FCSTD DOCUMENT  (FreeCAD 0.20R29177 +426 (Git))
Label: sketching
License: All rights reserved
LicenseURL: http://en.wikipedia.org/wiki/All_rights_reserved
objects: Sketcher::SketchObject×1
note: 1 computed .brp shape members not serialized (recipe doc carries the construction recipe); baked Part::Feature solids carry a one-line shape summary decoded from their .brp

FEATURE [Sketcher::SketchObject] Sketch
  FullyConstrained = false
  sketch-geometry (15):
    g0: LineSegment StartX=0 StartY=0 StartZ=0 EndX=-26.386 EndY=-14.4782 EndZ=0
    g1: LineSegment StartX=0 StartY=0 StartZ=0 EndX=-27.4681 EndY=14.59 EndZ=0
    g2: LineSegment StartX=0 StartY=0 StartZ=0 EndX=20.6994 EndY=22.0227 EndZ=0
    g3: LineSegment StartX=0 StartY=0 StartZ=0 EndX=30.9074 EndY=-5.00945 EndZ=0
    g4: LineSegment StartX=0 StartY=0 StartZ=0 EndX=5.19849 EndY=-29.7732 EndZ=0
    g5: Circle CenterX=0 CenterY=0 CenterZ=0 NormalX=0 NormalY=0 NormalZ=1 AngleXU=0 Radius=10.5414
    g6: ArcOfCircle CenterX=-26.386 CenterY=-14.4782 CenterZ=0 NormalX=0 NormalY=0 NormalZ=1 AngleXU=0 Radius=6.41713 StartAngle=2.35262 EndAngle=5.5881
    g7: ArcOfCircle CenterX=5.19849 CenterY=-29.7732 CenterZ=0 NormalX=0 NormalY=0 NormalZ=1 AngleXU=0 Radius=6.93275 StartAngle=3.33364 EndAngle=6.45538
    g8: ArcOfCircle CenterX=30.9074 CenterY=-5.00945 CenterZ=0 NormalX=0 NormalY=0 NormalZ=1 AngleXU=0 Radius=7.77119 StartAngle=4.39064 EndAngle=7.83271
    g9: ArcOfCircle CenterX=20.6994 CenterY=22.0227 CenterZ=0 NormalX=0 NormalY=0 NormalZ=1 AngleXU=0 Radius=9.12477 StartAngle=5.58579 EndAngle=8.96771
    g10: ArcOfCircle CenterX=-27.4681 CenterY=14.59 CenterZ=0 NormalX=0 NormalY=0 NormalZ=1 AngleXU=0 Radius=8.2668 StartAngle=0.742739 EndAngle=4.1801
    g11: ArcOfCircle CenterX=-6.52174 CenterY=27.6938 CenterZ=0 NormalX=0 NormalY=0 NormalZ=1 AngleXU=0 Radius=16.7422 StartAngle=3.80515 EndAngle=6.17003
    g12: ArcOfCircle CenterX=-45.0851 CenterY=-1.22873 CenterZ=0 NormalX=0 NormalY=0 NormalZ=1 AngleXU=0 Radius=15.7627 StartAngle=6.1871 EndAngle=7.29849
    g13: ArcOfCircle CenterX=-18.2031 CenterY=-35.0662 CenterZ=0 NormalX=0 NormalY=0 NormalZ=1 AngleXU=0 Radius=16.3255 StartAngle=0.349134 EndAngle=1.80789
    g14: ArcOfCircle CenterX=29.017 CenterY=-28.2609 CenterZ=0 NormalX=0 NormalY=0 NormalZ=1 AngleXU=0 Radius=13.2662 StartAngle=1.6421 EndAngle=3.06176
  constraints (11):
    c: Coincident(g0,g-1)
    c: Coincident(g1,g0)
    c: Coincident(g2,g0)
    c: Coincident(g3,g0)
    c: Coincident(g4,g0)
    c: Coincident(g6,g0)
    c: Coincident(g7,g4)
    c: Coincident(g8,g3)
    c: Coincident(g9,g2)
    c: Coincident(g10,g1)
    c: PointOnObject(g13,g6)
